# Revit family: STS-476 Панель индикации и управления__RV17_LOD400
name_source: partatom
category: Устройства вызова и оповещения
revit_build: Autodesk Revit 2017 (Build: 20170118_1100(x64)
units: mm (PartAtom-declared; Revit-internal decimal feet)

## family parameters
Всегда вертикально = Нет
На основе рабочей плоскости = Нет
Общий = Нет
При загрузке вырезать с полостями = Нет
Размер круглого соединителя = Использовать диаметр
Сохранять ориентацию аннотаций = Нет
Тип детали = Нормальный
Точка расчета площади = Нет

## types (1)
- STS-476 Панель индикации и управления
    ADSK_URL страницы изделия = https://stilsoft.ru
    ADSK_Единица измерения = шт.
    ADSK_Завод-изготовитель = ООО «Основа Безопасности»
    ADSK_Количество = 1
    ADSK_Масса = 1.2
    ADSK_Наименование = Панель индикации и управления STS-476
    ADSK_Размер_Высота = 21 мм
    ADSK_Размер_Длина = 283 мм
    ADSK_Размер_Ширина = 195 мм
    d_короба = 20 мм
    Диапазон рабочих температур, <unrecoverable-encoding: 5 bytes ef82b0d0a1> = от -10 до +40
    Количество разделов, шт. = 32
    Максимальная потребляемая мощность, не более, Вт = 13
    Максимальное количество аналоговых шлейфов в одном разделе, шт. = 16
    Максимальное количество записей в журнале, не менее, шт. = 10000
    Максимальное количество подключаемых охранных приемноконтрольных приборов, шт. = 8
    Напряжение электропитания постоянного тока, В = РоЕ (802.3af)
    Общее количество пользователей, до, шт. = 70
    Стандарт интерфейса связи = 10M/100M Ethernet (1 разъем RJ45)
10M/100M Ethernet (1 разъем RJ45)
10M/100M Ethernet (1 разъем RJ45)
